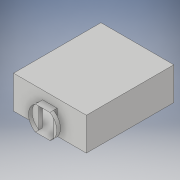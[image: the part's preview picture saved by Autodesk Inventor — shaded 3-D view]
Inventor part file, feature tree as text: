
AUTODESK INVENTOR PART (.ipt)
format: ipt  version: 2017 (Build 210142000, 142)  size: 165,888 bytes
history: native  units: in
note: dims shown in document units (in); Inventor stores cm internally (conversion verified against a paired STEP export)
features: extrude x5, sketch x5, delete_face x1
ambient origin geometry x8: Origin, YZ Plane, XZ Plane, XY Plane, X Axis, Y Axis, Z Axis, Center Point
bodies: Solid1 (feature_tree)
feature tree (11):
  extrude  "floor"  Depth=22.0in
  extrude  "walls"  Depth=1.0in
  extrude  "doorframe"  Depth=1.0in
  extrude  "ceiling"  Depth=1.0in TaperAngle=0.0deg
  extrude  "connection"  Depth=6.6667in
  delete_face  "Delete Face2"
  sketch  "Sketch1"  dims[d0=22.0in d1=26.0in]
  sketch  "Sketch4"  dims[d2=1.0in d3=0.0in d11=1.0in]
  sketch  "Sketch5"  dims[d12=1.0in d13=1.0in]
  sketch  "Sketch7"  dims[d14=1.0in d15=10.0in d16=0.0in]
  sketch  "Sketch12"  dims[d17=2.0in d18=6.6667in d20=8.6667in d21=0.0in d22=1.0in d23=0.0in d37=6.6667in d79=4.0in d80=3.8873in d81=3.8873in d82=1.6458in d83=3.3333in d84=1.0in d85=1.0in d86=1.0in d87=1.0in d88=0.0in]
